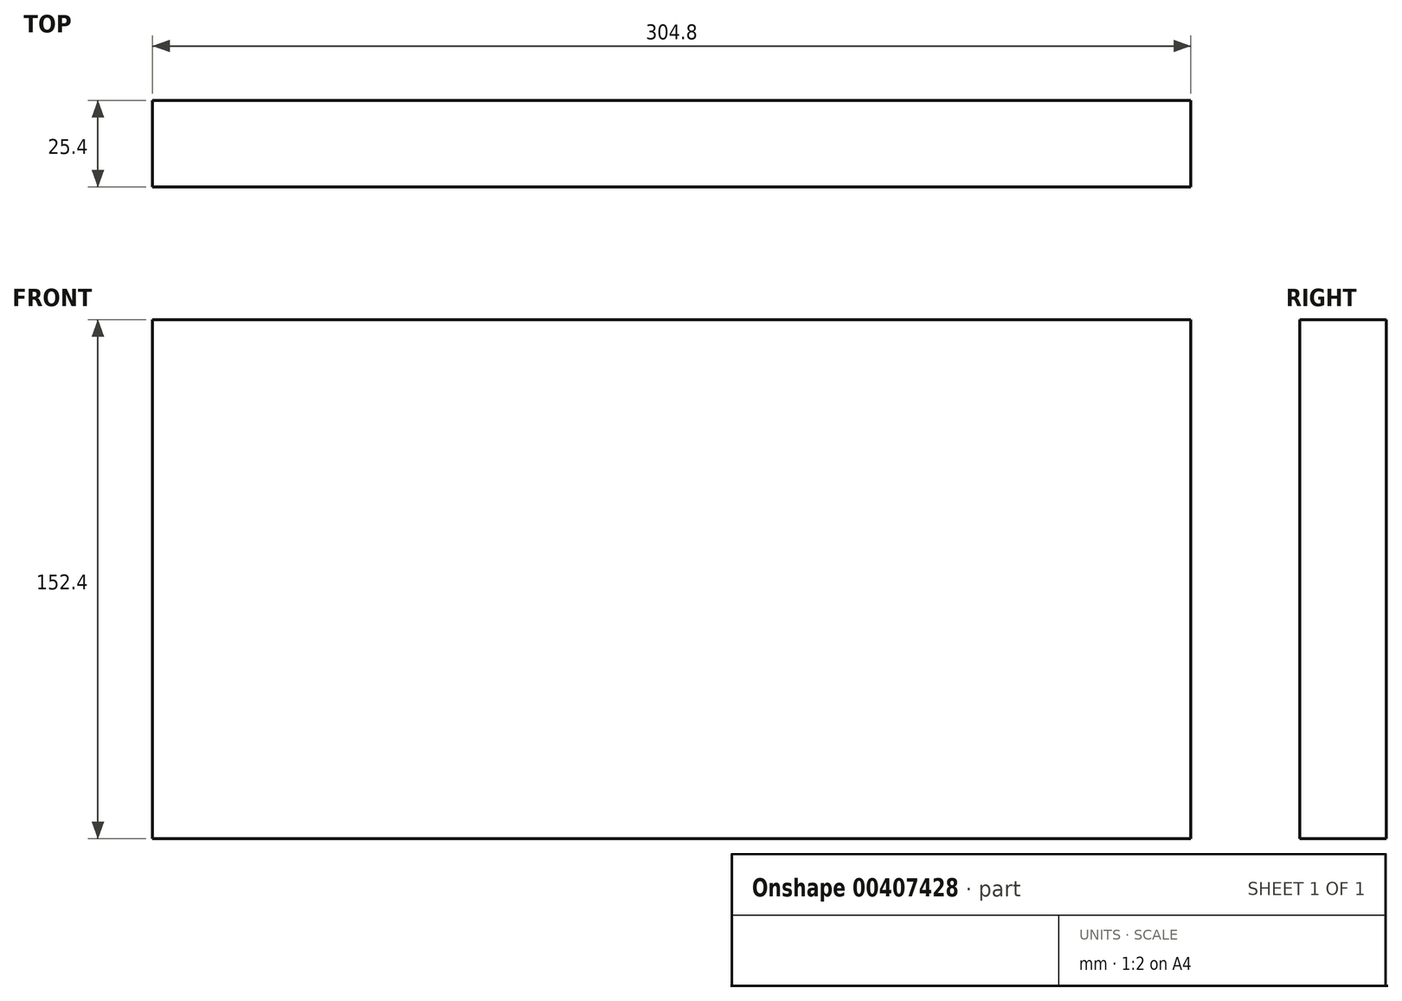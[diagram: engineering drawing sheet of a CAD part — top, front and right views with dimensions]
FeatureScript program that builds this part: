
annotation { "Feature Type Name" : "Feature", "Feature Type Description" : "" }
export const myFeature = defineFeature(function(context is Context, id is Id, definition is map)
    precondition{}
    {
        {
            var Q0;
            Q0=qCreatedBy(makeId("Front.planeOp"),FACE);
            var sketch = newSketch(context, id + "F0", { "sketchPlane" : qUnion([Q0])});
            skLineSegment(sketch, "E0.bottom", {"start": v(-171, 119.5) * mm, "end": v(133.8, 119.5) * mm});
            skLineSegment(sketch, "E0.top", {"start": v(-171, -32.9) * mm, "end": v(133.8, -32.9) * mm});
            skLineSegment(sketch, "E0.left", {"start": v(-171, 119.5) * mm, "end": v(-171, -32.9) * mm});
            skLineSegment(sketch, "E0.right", {"start": v(133.8, 119.5) * mm, "end": v(133.8, -32.9) * mm});
            skSolve(sketch);
        }
        {
            var Q0;
            Q0=makeQuery(id+"F0.imprint","IMPRINT",FACE,{"disambiguationData":[TD([[makeQuery(id+"F0.imprint","IMPRINT",EDGE,{"derivedFrom":sQuery(id+"F0.wireOp",EDGE,"E0.bottom")}),-1.0]])]});
            extrude(context, id + "F1", {"entities" : qUnion([Q0]), "depth" : 25.4 * mm});
        }
    });
